# Revit family: Classic Sink or Font mountable tap
name_source: partatom
category: Generic Models
revit_build: Autodesk Revit MEP 2013 (Build: 20130531_2115(x64)
units: mm (PartAtom-declared; Revit-internal decimal feet)

## types (24) — shared parameters
Manufacturer = Zip Industries Ltd
Product Range = Hydrotap
URL = www.zipindustries.co.uk
WRAS Approved = Yes

## per-type parameters (varying)
| type | Model | Tap Colour |
| Hydrotap Classic - 91519UK (Bright Chrome) |  |  |
| Hydrotap Classic - 91520UK (Bright Chrome) |  |  |
| Hydrotap Classic - 91522UK (Bright Chrome) |  |  |
| Hydrotap Classic - 91521UK (Bright Chrome) |  |  |
| Hydrotap Classic - 91518UK (Bright Chrome) |  |  |
| Hydrotap Classic - 91517UK (Bright Chrome) |  |  |
| Hydrotap Classic - 91566UK (Brushed Chrome) |  |  |
| Hydrotap Classic - 91569UK (Brushed Chrome) |  |  |
| Hydrotap Classic - 91592UK (Brushed Chrome) |  |  |
| Hydrotap Classic - 91589UK (Brushed Chrome) |  |  |
| Hydrotap Classic - 91586UK (Brushed Chrome) |  |  |
| Hydrotap Classic - 91583UK (Brushed Chrome) |  | As per name List above |
| Hydrotap Classic - 91568UK (Gloss Black) |  | As per name List above |
| Hydrotap Classic - 91570UK (Gloss Black) |  | As per name List above |
| Hydrotap Classic - 91593UK (Gloss Black) |  | As per name List above |
| Hydrotap Classic - 91590UK (Gloss Black) |  | As per name List above |
| Hydrotap Classic - 91587UK (Gloss Black) |  | As per name List above |
| Hydrotap Classic - 91584UK (Gloss Black) |  | As per name List above |
| Hydrotap Classic - 91581UK (Matt Black) |  | As per name List above |
| Hydrotap Classic - 91582UK (Matt Black) |  | As per name List above |
| Hydrotap Classic - 91594UK (Matt Black) |  | As per name List above |
| Hydrotap Classic - 91591UK (Matt Black) |  | As per name List above |
| Hydrotap Classic - 91588UK (Matt Black) |  | As per name List above |
| HydroTap Classic | G4 Classic range | As per name List above |
